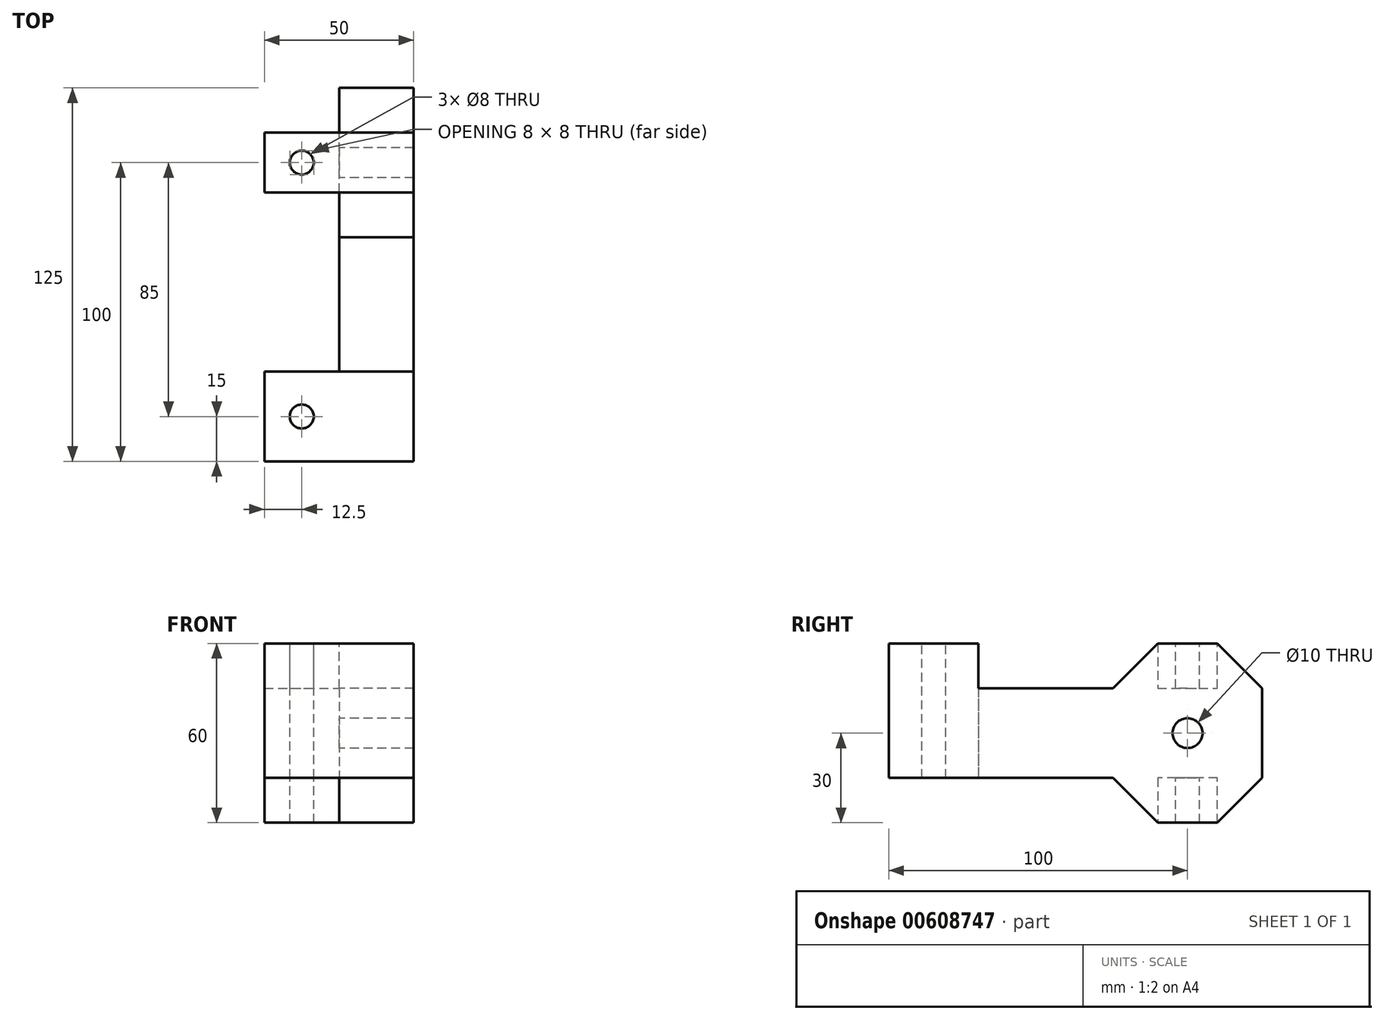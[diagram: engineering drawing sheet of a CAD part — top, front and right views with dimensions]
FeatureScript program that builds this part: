
annotation { "Feature Type Name" : "Feature", "Feature Type Description" : "" }
export const myFeature = defineFeature(function(context is Context, id is Id, definition is map)
    precondition{}
    {
        {
            var Q0;
            Q0=qCreatedBy(makeId("Right.planeOp"),FACE);
            var sketch = newSketch(context, id + "F0", { "sketchPlane" : qUnion([Q0])});
            skCircle(sketch, "E0", {"center": v(0, 0) * mm, "radius": 5 * mm});
            skLineSegment(sketch, "E1.0", {"start": v(10, -30) * mm, "end": v(-10, -30) * mm});
            skLineSegment(sketch, "E1.1", {"start": v(-10, -30) * mm, "end": v(-25, -15) * mm});
            skLineSegment(sketch, "E1.3", {"start": v(-25, 15) * mm, "end": v(-10, 30) * mm});
            skLineSegment(sketch, "E1.4", {"start": v(-10, 30) * mm, "end": v(10, 30) * mm});
            skLineSegment(sketch, "E1.5", {"start": v(10, 30) * mm, "end": v(25, 15) * mm});
            skLineSegment(sketch, "E1.6", {"start": v(25, 15) * mm, "end": v(25, -15) * mm});
            skLineSegment(sketch, "E1.7", {"start": v(25, -15) * mm, "end": v(10, -30) * mm});
            skPoint(sketch, "E1.0.midPoint", {"position": v(0, -30) * mm});
            skLineSegment(sketch, "E2", {"start": v(-25, 15) * mm, "end": v(-100, 15) * mm});
            skLineSegment(sketch, "E3", {"start": v(-100, 15) * mm, "end": v(-100, -15) * mm});
            skLineSegment(sketch, "E4", {"start": v(-100, -15) * mm, "end": v(-25, -15) * mm});
            skSolve(sketch);
        }
        {
            var Q0;
            Q0=makeQuery(id+"F0.imprint","IMPRINT",FACE,{"disambiguationData":[TD([[makeQuery(id+"F0.imprint","IMPRINT",EDGE,{"derivedFrom":sQuery(id+"F0.wireOp",EDGE,"E0")}),-1.0]])]});
            extrude(context, id + "F1", {"entities" : qUnion([Q0]), "depth" : 25 * mm, "offsetDistance" : 25 * mm});
        }
        {
            var Q0;
            Q0=makeQuery(id+"F1.opExtrude","CAP_FACE",FACE,{"disambiguationData":[OSD([sQuery(id+"F0.wireOp",EDGE,"E0"),sQuery(id+"F0.wireOp",EDGE,"E1.0"),sQuery(id+"F0.wireOp",EDGE,"E1.1"),sQuery(id+"F0.wireOp",EDGE,"E1.3"),sQuery(id+"F0.wireOp",EDGE,"E1.4"),sQuery(id+"F0.wireOp",EDGE,"E1.5"),sQuery(id+"F0.wireOp",EDGE,"E1.6"),sQuery(id+"F0.wireOp",EDGE,"E1.7"),sQuery(id+"F0.wireOp",EDGE,"E2"),sQuery(id+"F0.wireOp",EDGE,"E3"),sQuery(id+"F0.wireOp",EDGE,"E4")])],"isStart":true});
            var sketch = newSketch(context, id + "F2", { "sketchPlane" : qUnion([Q0])});
            skLineSegment(sketch, "E5", {"start": v(-10, 30) * mm, "end": v(10, 30) * mm});
            skLineSegment(sketch, "E6", {"start": v(10, 30) * mm, "end": v(10, 15) * mm});
            skLineSegment(sketch, "E7", {"start": v(10, 15) * mm, "end": v(-10, 15) * mm});
            skLineSegment(sketch, "E8", {"start": v(-10, 15) * mm, "end": v(-10, 30) * mm});
            skLineSegment(sketch, "E9", {"start": v(-10, -15) * mm, "end": v(10, -15) * mm});
            skLineSegment(sketch, "E10", {"start": v(10, -15) * mm, "end": v(10, -30) * mm});
            skLineSegment(sketch, "E11", {"start": v(10, -30) * mm, "end": v(-10, -30) * mm});
            skLineSegment(sketch, "E12", {"start": v(-10, -30) * mm, "end": v(-10, -15) * mm});
            skLineSegment(sketch, "E13.left", {"start": v(100, 15) * mm, "end": v(100, -15) * mm});
            skLineSegment(sketch, "E14", {"start": v(70, 15) * mm, "end": v(70, -15) * mm});
            skLineSegment(sketch, "E15", {"start": v(70, -15) * mm, "end": v(100, -15) * mm});
            skLineSegment(sketch, "E16", {"start": v(70, 15) * mm, "end": v(100, 15) * mm});
            skSolve(sketch);
        }
        {
            var Q0;
            Q0=makeQuery(id+"F2.imprint","IMPRINT",FACE,{"disambiguationData":[TD([[makeQuery(id+"F2.imprint","IMPRINT",EDGE,{"derivedFrom":sQuery(id+"F2.wireOp",EDGE,"E5")}),1.0]])]});
            var Q1;
            Q1=makeQuery(id+"F2.imprint","IMPRINT",FACE,{"disambiguationData":[TD([[makeQuery(id+"F2.imprint","IMPRINT",EDGE,{"derivedFrom":sQuery(id+"F2.wireOp",EDGE,"E9")}),-1.0]])]});
            var Q2;
            Q2=makeQuery(id+"F2.imprint","IMPRINT",FACE,{"disambiguationData":[TD([[makeQuery(id+"F2.imprint","IMPRINT",EDGE,{"derivedFrom":sQuery(id+"F2.wireOp",EDGE,"E13.left")}),-1.0]])]});
            extrude(context, id + "F3", {"entities" : qUnion([Q0, Q1, Q2]), "operationType" : NewBodyOperationType.ADD, "depth" : 25 * mm, "offsetDistance" : 25 * mm});
        }
        {
            var Q0;
            Q0=makeQuery(id+"F3.boolean.opBoolean","MERGE",FACE,{"derivedFrom":[makeQuery(id+"F1.opExtrude","SWEPT_FACE",FACE,{"disambiguationData":[OSD([sQuery(id+"F0.wireOp",EDGE,"E1.4")])]}),makeQuery(id+"F3.opExtrude","SWEPT_FACE",FACE,{"disambiguationData":[OSD([sQuery(id+"F2.wireOp",EDGE,"E5")])]})]});
            var sketch = newSketch(context, id + "F4", { "sketchPlane" : qUnion([Q0])});
            skCircle(sketch, "E17", {"center": v(-12.5, 0) * mm, "radius": 4 * mm});
            skSolve(sketch);
        }
        {
            var Q0;
            Q0=sQuery(id+"F4.wireOp",VERTEX,"E17.center");
            var Q1;
            Q1=makeQuery(id+"F1.opExtrude","SWEPT_BODY",BODY,{"disambiguationData":[OSD([sQuery(id+"F0.wireOp",EDGE,"E0"),sQuery(id+"F0.wireOp",EDGE,"E1.0"),sQuery(id+"F0.wireOp",EDGE,"E1.1"),sQuery(id+"F0.wireOp",EDGE,"E1.3"),sQuery(id+"F0.wireOp",EDGE,"E1.4"),sQuery(id+"F0.wireOp",EDGE,"E1.5"),sQuery(id+"F0.wireOp",EDGE,"E1.6"),sQuery(id+"F0.wireOp",EDGE,"E1.7"),sQuery(id+"F0.wireOp",EDGE,"E2"),sQuery(id+"F0.wireOp",EDGE,"E3"),sQuery(id+"F0.wireOp",EDGE,"E4")])]});
            hole(context, id + "F5", {"style" : HoleStyle.SIMPLE, "endStyle" : HoleEndStyle.THROUGH, "holeDiameter" : 8 * mm, "majorDiameter" : 5 * mm, "isTappedThrough" : true, "tappedDepth" : 12 * mm, "tapClearance" : 3, "locations" : qUnion([Q0]), "scope" : qUnion([Q1])});
        }
        {
            var Q0;
            Q0=makeQuery(id+"F1.opExtrude","SWEPT_FACE",FACE,{"disambiguationData":[OSD([sQuery(id+"F0.wireOp",EDGE,"E2")])]});
            var sketch = newSketch(context, id + "F6", { "sketchPlane" : qUnion([Q0])});
            skCircle(sketch, "E18", {"center": v(-12.5, -85) * mm, "radius": 4 * mm});
            skLineSegment(sketch, "E19.bottom", {"start": v(-25, -70) * mm, "end": v(25, -70) * mm});
            skLineSegment(sketch, "E19.top", {"start": v(-25, -100) * mm, "end": v(25, -100) * mm});
            skLineSegment(sketch, "E19.left", {"start": v(-25, -70) * mm, "end": v(-25, -100) * mm});
            skLineSegment(sketch, "E19.right", {"start": v(25, -70) * mm, "end": v(25, -100) * mm});
            skSolve(sketch);
        }
        {
            var Q0;
            Q0=sQuery(id+"F6.wireOp",VERTEX,"E18.center");
            var Q1;
            Q1=makeQuery(id+"F1.opExtrude","SWEPT_BODY",BODY,{"disambiguationData":[OSD([sQuery(id+"F0.wireOp",EDGE,"E0"),sQuery(id+"F0.wireOp",EDGE,"E1.0"),sQuery(id+"F0.wireOp",EDGE,"E1.1"),sQuery(id+"F0.wireOp",EDGE,"E1.3"),sQuery(id+"F0.wireOp",EDGE,"E1.4"),sQuery(id+"F0.wireOp",EDGE,"E1.5"),sQuery(id+"F0.wireOp",EDGE,"E1.6"),sQuery(id+"F0.wireOp",EDGE,"E1.7"),sQuery(id+"F0.wireOp",EDGE,"E2"),sQuery(id+"F0.wireOp",EDGE,"E3"),sQuery(id+"F0.wireOp",EDGE,"E4")])]});
            hole(context, id + "F7", {"style" : HoleStyle.SIMPLE, "endStyle" : HoleEndStyle.THROUGH, "holeDiameter" : 8 * mm, "majorDiameter" : 5 * mm, "isTappedThrough" : true, "tappedDepth" : 12 * mm, "tapClearance" : 3, "locations" : qUnion([Q0]), "scope" : qUnion([Q1])});
        }
        {
            var Q0;
            Q0=makeQuery(id+"F6.imprint","IMPRINT",FACE,{"disambiguationData":[TD([[makeQuery(id+"F6.imprint","IMPRINT",EDGE,{"derivedFrom":sQuery(id+"F6.wireOp",EDGE,"E18")}),-1.0]])]});
            extrude(context, id + "F8", {"entities" : qUnion([Q0]), "operationType" : NewBodyOperationType.ADD, "depth" : 15 * mm, "offsetDistance" : 25 * mm});
        }
    });
